# Revit family: Caroma Cube 0.8L Electronic Urinal
name_source: partatom
category: Plumbing Fixtures
revit_build: Autodesk Revit LT 2014 (Build: 20130308_1515(x64)
units: mm (PartAtom-declared; Revit-internal decimal feet)

## types (1)
- Standard
    Assembly Code = C1030210
    CW Connection = Yes
    CWFU = 0.25
    Cost = 0 $
    Default Elevation = 610 mm  [stored 2.00131 ft]
    Description = Caroma Cube 0.8L Electronic Urinal
    HW Connection = No
    Hardware = Metal-Chrome-Caroma
    Height_ANZRS = 670 mm  [stored 2.19816 ft]
    Keynote = UR
    Length_ANZRS = 260 mm  [stored 0.853018 ft]
    Manufacturer = GWA Bathrooms & Kitchens
    Material_ANZRS = Porcelain-White-Caroma
    Model = 687663W
    ModifiedIssue_ANZRS = 20140916 $
    PlumbingMaterial_ANZRS = Porcelain-White-Caroma
    Type Comments = Urine sensing technology, stadium mode, hygiene flush every 24 hours
    URL = http://www.caroma.com.au
    Vent Connection = No
    WELSRating_ANZRS = WELS 6 Star rated, 0.8L
    WFU = 0.25
    Waste Connection = Yes
    Width_ANZRS = 345 mm  [stored 1.13189 ft]

note: [stored X ft] marks values corroborated as IEEE doubles in the binary element streams (Revit-internal decimal feet)

## geometry (parser evidence)
native form markers: Blend x16, Sweep x1
no freeform markers — native parametric forms only
